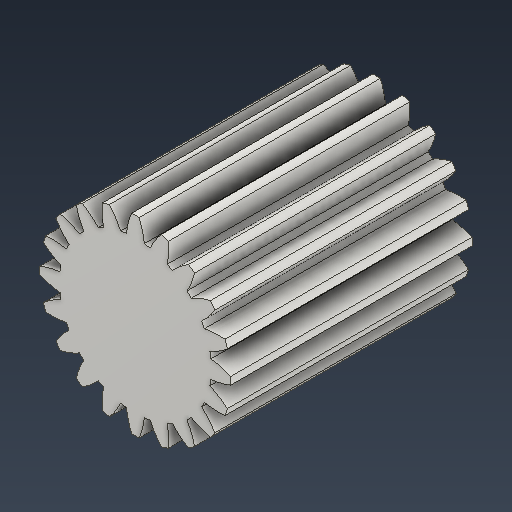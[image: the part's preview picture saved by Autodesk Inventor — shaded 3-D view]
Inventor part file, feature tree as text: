
AUTODESK INVENTOR PART (.ipt)
format: ipt  version: 2021 (Build 250183000, 183)  size: 284,160 bytes
history: native  units: mm (DEFAULTED — no unit token found)
features: plane x3, other x3, sketch x2, extrude x1
ambient origin geometry x8: Origin, YZ Plane, XZ Plane, XY Plane, X Axis, Y Axis, Z Axis, Center Point
bodies: Solid1 (feature_tree)
feature tree (9):
  extrude  "Extrusion1"  Depth=2.5mm TaperAngle=0.0deg
  plane  "Work Plane2"
  plane  "Work Plane8"
  plane  "Work Plane9"
  other  "Engrenagem reta"
  sketch  "Sketch1"  dims[d0=1.979988mm d1=2.5mm d2=0.0mm]
  sketch  "Sketch2"  dims[d3=1.8mm d4=10.0mm d5=0.0mm d16=3.597588mm d17=0.0mm d34=1.570796mm d39=0.0mm d41=0.0mm d43=3.597588mm d46=3.597588mm d47=0.0mm d48=0.0mm]
  other  "Srf1"
  other  "Diâmetro do flanco"
